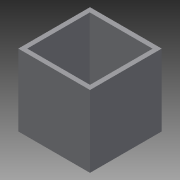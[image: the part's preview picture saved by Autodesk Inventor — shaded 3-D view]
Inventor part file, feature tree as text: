
AUTODESK INVENTOR PART (.ipt)
format: ipt  version: 2015 (Build 190159000, 159)  size: 82,944 bytes
history: native  units: in
note: dims shown in document units (in); Inventor stores cm internally (conversion verified against a paired STEP export)
features: extrude x2, sketch x2
ambient origin geometry x8: Origin, YZ Plane, XZ Plane, XY Plane, X Axis, Y Axis, Z Axis, Center Point
bodies: Solid1 (feature_tree)
feature tree (4):
  extrude  "Extrusion1"  Depth=4.0in
  extrude  "Extrusion2"  Depth=3.75in TaperAngle=0.0deg
  sketch  "Sketch1"  dims[d0=4.0in d1=4.0in]
  sketch  "Sketch2"  dims[d2=0.25in d3=0.0in d8=3.75in d9=0.0in]
